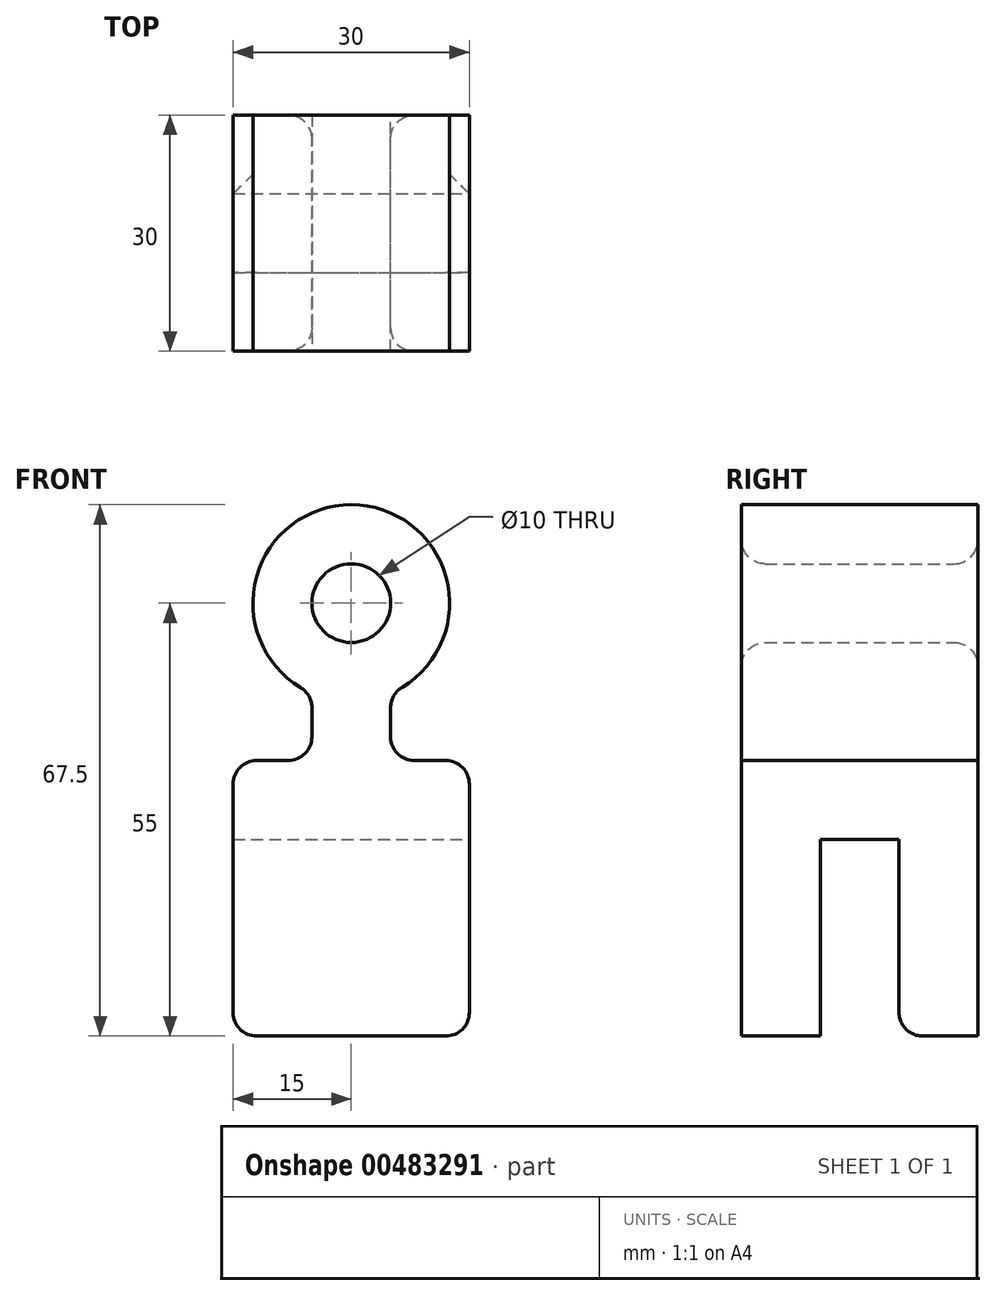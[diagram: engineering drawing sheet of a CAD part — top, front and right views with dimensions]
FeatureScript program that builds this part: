
annotation { "Feature Type Name" : "Feature", "Feature Type Description" : "" }
export const myFeature = defineFeature(function(context is Context, id is Id, definition is map)
    precondition{}
    {
        {
            var Q0;
            Q0=qCreatedBy(makeId("Front.planeOp"),FACE);
            var sketch = newSketch(context, id + "F0", { "sketchPlane" : qUnion([Q0])});
            skLineSegment(sketch, "E0.bottom", {"start": v(0, 0) * mm, "end": v(30, 0) * mm});
            skLineSegment(sketch, "E0.top", {"start": v(0, 35) * mm, "end": v(30, 35) * mm});
            skLineSegment(sketch, "E0.left", {"start": v(0, 0) * mm, "end": v(0, 35) * mm});
            skLineSegment(sketch, "E0.right", {"start": v(30, 0) * mm, "end": v(30, 35) * mm});
            skPoint(sketch, "E1", {"position": v(15, 35) * mm});
            skLineSegment(sketch, "E2", {"start": v(15, 35) * mm, "end": v(15, 68.04) * mm, "construction": true});
            skLineSegment(sketch, "E3.top", {"start": v(10, 35) * mm, "end": v(20, 35) * mm});
            skLineSegment(sketch, "E3.left", {"start": v(10, 43.54) * mm, "end": v(10, 35) * mm});
            skLineSegment(sketch, "E3.right", {"start": v(20, 43.54) * mm, "end": v(20, 35) * mm});
            skArc(sketch, "E4", {"start": v(20, 43.54) * mm, "mid": v(15, 67.5) * mm, "end": v(10, 43.54) * mm});
            skCircle(sketch, "E5", {"center": v(15, 55) * mm, "radius": 5 * mm});
            skSolve(sketch);
        }
        {
            var Q0;
            Q0 = qSketchRegion(id + "F0", true);
            extrude(context, id + "F1", {"entities" : qUnion([Q0]), "depth" : 30 * mm});
        }
        {
            var Q0;
            Q0=makeQuery(id+"F1.opExtrude","SWEPT_FACE",FACE,{"disambiguationData":[OSD([sQuery(id+"F0.wireOp",EDGE,"E0.right")])]});
            var sketch = newSketch(context, id + "F2", { "sketchPlane" : qUnion([Q0])});
            skLineSegment(sketch, "E6.bottom", {"start": v(-20, 0) * mm, "end": v(-10, 0) * mm});
            skLineSegment(sketch, "E6.top", {"start": v(-20, 25) * mm, "end": v(-10, 25) * mm});
            skLineSegment(sketch, "E6.left", {"start": v(-20, 0) * mm, "end": v(-20, 25) * mm});
            skLineSegment(sketch, "E6.right", {"start": v(-10, 0) * mm, "end": v(-10, 25) * mm});
            skSolve(sketch);
        }
        {
            var Q0;
            Q0 = qSketchRegion(id + "F2", true);
            extrude(context, id + "F3", {"entities" : qUnion([Q0]), "operationType" : NewBodyOperationType.REMOVE, "endBound" : BoundingType.THROUGH_ALL, "oppositeDirection" : true, "depth" : 25 * mm});
        }
        {
            var Q0;
            Q0=makeQuery(id+"F1.opExtrude","CAP_EDGE",EDGE,{"disambiguationData":[OSD([sQuery(id+"F0.wireOp",EDGE,"E5")])],"isStart":false});
            var Q1;
            Q1=makeQuery(id+"F1.opExtrude","CAP_EDGE",EDGE,{"disambiguationData":[OSD([sQuery(id+"F0.wireOp",EDGE,"E5")])],"isStart":true});
            var Q2;
            Q2=makeQuery(id+"F1.opExtrude","SWEPT_EDGE",EDGE,{"disambiguationData":[OSD([sQuery(id+"F0.wireOp",EDGE,"E3.right"),sQuery(id+"F0.wireOp",EDGE,"E4")])]});
            var Q3;
            Q3=makeQuery(id+"F1.opExtrude","SWEPT_EDGE",EDGE,{"disambiguationData":[OSD([sQuery(id+"F0.wireOp",EDGE,"E0.top"),sQuery(id+"F0.wireOp",EDGE,"E3.top"),sQuery(id+"F0.wireOp",EDGE,"E3.right")])]});
            var Q4;
            Q4=makeQuery(id+"F1.opExtrude","SWEPT_EDGE",EDGE,{"disambiguationData":[OSD([sQuery(id+"F0.wireOp",EDGE,"E0.top"),sQuery(id+"F0.wireOp",EDGE,"E3.top"),sQuery(id+"F0.wireOp",EDGE,"E3.left")])]});
            var Q5;
            Q5=makeQuery(id+"F1.opExtrude","SWEPT_EDGE",EDGE,{"disambiguationData":[OSD([sQuery(id+"F0.wireOp",EDGE,"E3.left"),sQuery(id+"F0.wireOp",EDGE,"E4")])]});
            var Q6;
            Q6=makeQuery(id+"F1.opExtrude","SWEPT_EDGE",EDGE,{"disambiguationData":[OSD([sQuery(id+"F0.wireOp",EDGE,"E0.top"),sQuery(id+"F0.wireOp",EDGE,"E0.right")])]});
            var Q7;
            Q7=makeQuery(id+"F1.opExtrude","SWEPT_EDGE",EDGE,{"disambiguationData":[OSD([sQuery(id+"F0.wireOp",EDGE,"E0.top"),sQuery(id+"F0.wireOp",EDGE,"E0.left")])]});
            var Q8;
            {var subQ0=sQuery(id+"F0.wireOp",EDGE,"E0.bottom");var subQ1=sQuery(id+"F0.wireOp",EDGE,"E0.right");Q8=makeQuery(id+"F3.boolean.opBoolean","SPLIT",EDGE,{"disambiguationData":[TD([makeQuery(id+"F3.opExtrude","SWEPT_FACE",FACE,{"disambiguationData":[OSD([sQuery(id+"F2.wireOp",EDGE,"E6.left")])]})])],"derivedFrom":makeQuery(id+"F1.opExtrude","SWEPT_EDGE",EDGE,{"disambiguationData":[OSD([subQ0,subQ1])]})});}
            var Q9;
            {var subQ0=sQuery(id+"F0.wireOp",EDGE,"E0.bottom");var subQ1=sQuery(id+"F0.wireOp",EDGE,"E0.right");Q9=makeQuery(id+"F3.boolean.opBoolean","SPLIT",EDGE,{"disambiguationData":[TD([makeQuery(id+"F3.opExtrude","SWEPT_FACE",FACE,{"disambiguationData":[OSD([sQuery(id+"F2.wireOp",EDGE,"E6.right")])]})])],"derivedFrom":makeQuery(id+"F1.opExtrude","SWEPT_EDGE",EDGE,{"disambiguationData":[OSD([subQ0,subQ1])]})});}
            var Q10;
            {var subQ0=sQuery(id+"F0.wireOp",EDGE,"E0.bottom");var subQ1=sQuery(id+"F0.wireOp",EDGE,"E0.left");Q10=makeQuery(id+"F3.boolean.opBoolean","SPLIT",EDGE,{"disambiguationData":[TD([makeQuery(id+"F3.opExtrude","SWEPT_FACE",FACE,{"disambiguationData":[OSD([sQuery(id+"F2.wireOp",EDGE,"E6.left")])]})])],"derivedFrom":makeQuery(id+"F1.opExtrude","SWEPT_EDGE",EDGE,{"disambiguationData":[OSD([subQ0,subQ1])]})});}
            var Q11;
            {var subQ0=sQuery(id+"F0.wireOp",EDGE,"E0.bottom");var subQ1=sQuery(id+"F0.wireOp",EDGE,"E0.left");Q11=makeQuery(id+"F3.boolean.opBoolean","SPLIT",EDGE,{"disambiguationData":[TD([makeQuery(id+"F3.opExtrude","SWEPT_FACE",FACE,{"disambiguationData":[OSD([sQuery(id+"F2.wireOp",EDGE,"E6.right")])]})])],"derivedFrom":makeQuery(id+"F1.opExtrude","SWEPT_EDGE",EDGE,{"disambiguationData":[OSD([subQ0,subQ1])]})});}
            var Q12;
            Q12=makeQuery(id+"F3.boolean.opBoolean","COPY",EDGE,{"derivedFrom":makeQuery(id+"F3.opExtrude","SWEPT_EDGE",EDGE,{"disambiguationData":[OSD([sQuery(id+"F0.wireOp",EDGE,"E0.bottom"),sQuery(id+"F0.wireOp",EDGE,"E0.right"),sQuery(id+"F2.wireOp",EDGE,"E6.bottom"),sQuery(id+"F2.wireOp",EDGE,"E6.left")])]})});
            var Q13;
            Q13=makeQuery(id+"F3.boolean.opBoolean","COPY",EDGE,{"derivedFrom":makeQuery(id+"F3.opExtrude","SWEPT_EDGE",EDGE,{"disambiguationData":[OSD([sQuery(id+"F0.wireOp",EDGE,"E0.bottom"),sQuery(id+"F0.wireOp",EDGE,"E0.right"),sQuery(id+"F2.wireOp",EDGE,"E6.bottom"),sQuery(id+"F2.wireOp",EDGE,"E6.right")])]})});
            fillet(context, id + "F4", {"entities" : qUnion([Q0, Q1, Q2, Q3, Q4, Q5, Q6, Q7, Q8, Q9, Q10, Q11, Q12, Q13]), "radius" : 3 * mm, "tangentPropagation" : true, "allowEdgeOverflow" : false});
        }
    });
